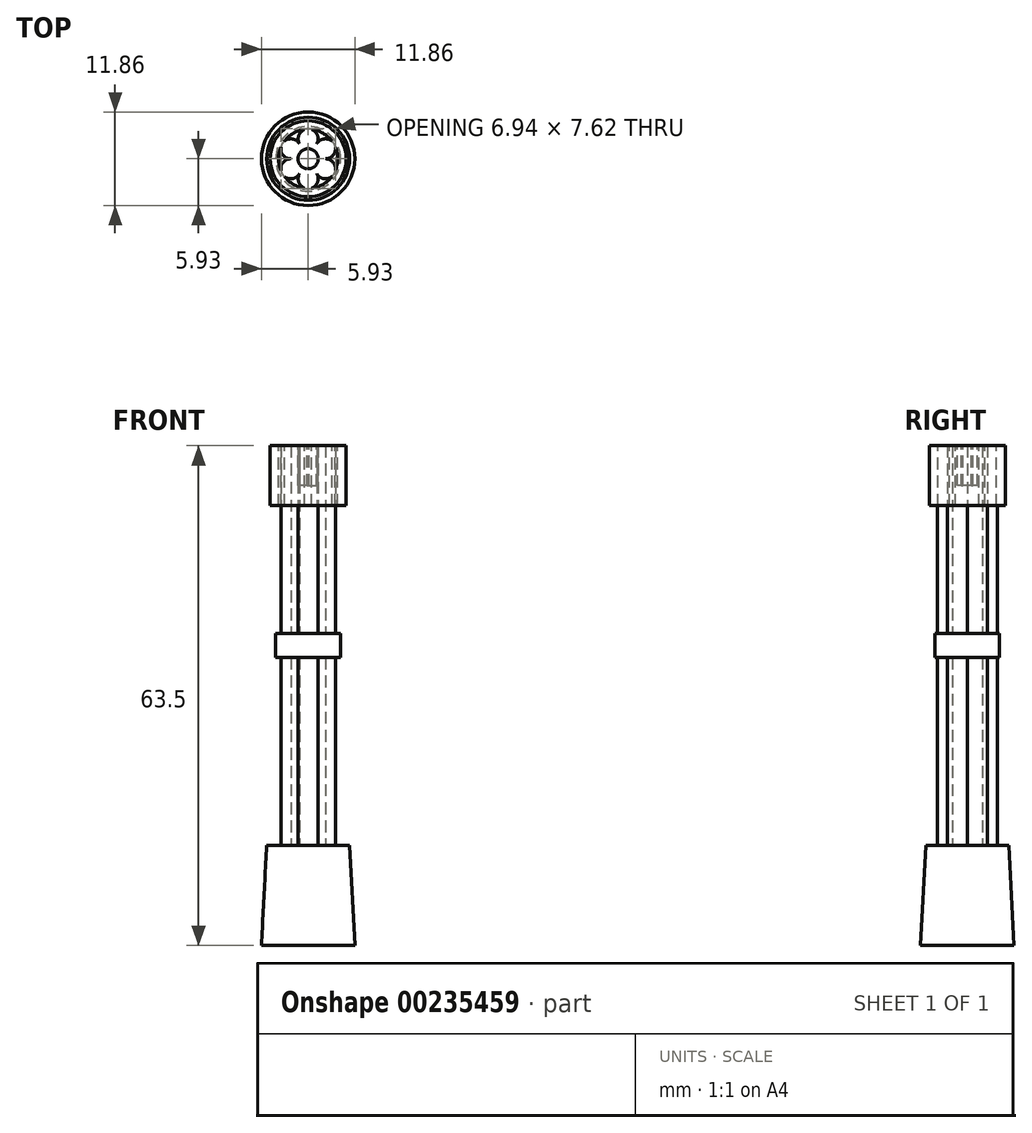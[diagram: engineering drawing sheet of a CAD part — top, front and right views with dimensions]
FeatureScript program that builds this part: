
annotation { "Feature Type Name" : "Feature", "Feature Type Description" : "" }
export const myFeature = defineFeature(function(context is Context, id is Id, definition is map)
    precondition{}
    {
        {
            var Q0;
            Q0=qCreatedBy(makeId("Top.planeOp"),FACE);
            var sketch = newSketch(context, id + "F0", { "sketchPlane" : qUnion([Q0])});
            skCircle(sketch, "E0", {"center": v(0, 0) * mm, "radius": 1.27 * mm});
            skCircle(sketch, "E1", {"center": v(0, 2.54) * mm, "radius": 1.27 * mm});
            skCircle(sketch, "E2.1.0", {"center": v(-2.2, 1.27) * mm, "radius": 1.27 * mm});
            skCircle(sketch, "E2.2.0", {"center": v(-2.2, -1.27) * mm, "radius": 1.27 * mm});
            skCircle(sketch, "E2.3.0", {"center": v(0, -2.54) * mm, "radius": 1.27 * mm});
            skCircle(sketch, "E2.4.0", {"center": v(2.2, -1.27) * mm, "radius": 1.27 * mm});
            skCircle(sketch, "E2.5.0", {"center": v(2.2, 1.27) * mm, "radius": 1.27 * mm});
            skCircle(sketch, "E3", {"center": v(0, 0) * mm, "radius": 3.81 * mm});
            skCircle(sketch, "E4", {"center": v(0, 0) * mm, "radius": 4.12 * mm});
            skSolve(sketch);
        }
        {
            var Q0;
            {var subQ0=sQuery(id+"F0.wireOp",EDGE,"E0");var subQ4=makeQuery(id+"F0.imprint","INTERSECT",VERTEX,{"derivedFrom":[subQ0,sQuery(id+"F0.wireOp",EDGE,"E1")]});Q0=makeQuery(id+"F0.imprint","IMPRINT",FACE,{"disambiguationData":[TD([[makeQuery(id+"F0.imprint","IMPRINT",EDGE,{"disambiguationData":[TD([[subQ4,1.0]])],"derivedFrom":subQ0}),1.0]])]});}
            var Q1;
            {var subQ0=sQuery(id+"F0.wireOp",EDGE,"E1");var subQ1=sQuery(id+"F0.wireOp",EDGE,"E0");var subQ2=makeQuery(id+"F0.imprint","INTERSECT",VERTEX,{"derivedFrom":[subQ1,subQ0]});Q1=makeQuery(id+"F0.imprint","IMPRINT",FACE,{"disambiguationData":[TD([[makeQuery(id+"F0.imprint","IMPRINT",EDGE,{"disambiguationData":[TD([[subQ2,-1.0]])],"derivedFrom":subQ1}),-1.0]])]});}
            var Q2;
            {var subQ0=sQuery(id+"F0.wireOp",EDGE,"E1");var subQ1=sQuery(id+"F0.wireOp",EDGE,"E0");var subQ2=makeQuery(id+"F0.imprint","INTERSECT",VERTEX,{"derivedFrom":[subQ1,subQ0]});Q2=makeQuery(id+"F0.imprint","IMPRINT",FACE,{"disambiguationData":[TD([[makeQuery(id+"F0.imprint","IMPRINT",EDGE,{"disambiguationData":[TD([[subQ2,1.0]])],"derivedFrom":subQ1}),-1.0]])]});}
            var Q3;
            {var subQ0=sQuery(id+"F0.wireOp",EDGE,"E2.5.0");var subQ1=sQuery(id+"F0.wireOp",EDGE,"E0");var subQ2=makeQuery(id+"F0.imprint","INTERSECT",VERTEX,{"derivedFrom":[subQ1,subQ0]});Q3=makeQuery(id+"F0.imprint","IMPRINT",FACE,{"disambiguationData":[TD([[makeQuery(id+"F0.imprint","IMPRINT",EDGE,{"disambiguationData":[TD([[subQ2,1.0]])],"derivedFrom":subQ1}),-1.0]])]});}
            var Q4;
            {var subQ0=sQuery(id+"F0.wireOp",EDGE,"E2.3.0");var subQ1=sQuery(id+"F0.wireOp",EDGE,"E0");var subQ2=makeQuery(id+"F0.imprint","INTERSECT",VERTEX,{"derivedFrom":[subQ1,subQ0]});Q4=makeQuery(id+"F0.imprint","IMPRINT",FACE,{"disambiguationData":[TD([[makeQuery(id+"F0.imprint","IMPRINT",EDGE,{"disambiguationData":[TD([[subQ2,-1.0]])],"derivedFrom":subQ1}),-1.0]])]});}
            var Q5;
            {var subQ0=sQuery(id+"F0.wireOp",EDGE,"E2.2.0");var subQ1=sQuery(id+"F0.wireOp",EDGE,"E0");var subQ2=makeQuery(id+"F0.imprint","INTERSECT",VERTEX,{"derivedFrom":[subQ1,subQ0]});Q5=makeQuery(id+"F0.imprint","IMPRINT",FACE,{"disambiguationData":[TD([[makeQuery(id+"F0.imprint","IMPRINT",EDGE,{"disambiguationData":[TD([[subQ2,-1.0]])],"derivedFrom":subQ1}),-1.0]])]});}
            var Q6;
            {var subQ0=sQuery(id+"F0.wireOp",EDGE,"E2.1.0");var subQ1=sQuery(id+"F0.wireOp",EDGE,"E0");var subQ2=makeQuery(id+"F0.imprint","INTERSECT",VERTEX,{"derivedFrom":[subQ1,subQ0]});Q6=makeQuery(id+"F0.imprint","IMPRINT",FACE,{"disambiguationData":[TD([[makeQuery(id+"F0.imprint","IMPRINT",EDGE,{"disambiguationData":[TD([[subQ2,-1.0]])],"derivedFrom":subQ1}),-1.0]])]});}
            var Q7;
            {var subQ0=sQuery(id+"F0.wireOp",EDGE,"E1");var subQ1=makeQuery(id+"F0.imprint","INTERSECT",VERTEX,{"derivedFrom":[subQ0,sQuery(id+"F0.wireOp",EDGE,"E2.1.0")]});Q7=makeQuery(id+"F0.imprint","IMPRINT",FACE,{"disambiguationData":[TD([[makeQuery(id+"F0.imprint","IMPRINT",EDGE,{"disambiguationData":[TD([[subQ1,1.0]])],"derivedFrom":subQ0}),1.0]])]});}
            var Q8;
            {var subQ0=sQuery(id+"F0.wireOp",EDGE,"E2.1.0");var subQ1=makeQuery(id+"F0.imprint","INTERSECT",VERTEX,{"derivedFrom":[subQ0,sQuery(id+"F0.wireOp",EDGE,"E2.2.0")]});Q8=makeQuery(id+"F0.imprint","IMPRINT",FACE,{"disambiguationData":[TD([[makeQuery(id+"F0.imprint","IMPRINT",EDGE,{"disambiguationData":[TD([[subQ1,1.0]])],"derivedFrom":subQ0}),1.0]])]});}
            var Q9;
            {var subQ0=sQuery(id+"F0.wireOp",EDGE,"E2.2.0");var subQ1=makeQuery(id+"F0.imprint","INTERSECT",VERTEX,{"derivedFrom":[subQ0,sQuery(id+"F0.wireOp",EDGE,"E2.3.0")]});Q9=makeQuery(id+"F0.imprint","IMPRINT",FACE,{"disambiguationData":[TD([[makeQuery(id+"F0.imprint","IMPRINT",EDGE,{"disambiguationData":[TD([[subQ1,1.0]])],"derivedFrom":subQ0}),1.0]])]});}
            var Q10;
            {var subQ0=sQuery(id+"F0.wireOp",EDGE,"E2.3.0");var subQ1=makeQuery(id+"F0.imprint","INTERSECT",VERTEX,{"derivedFrom":[subQ0,sQuery(id+"F0.wireOp",EDGE,"E2.4.0")]});Q10=makeQuery(id+"F0.imprint","IMPRINT",FACE,{"disambiguationData":[TD([[makeQuery(id+"F0.imprint","IMPRINT",EDGE,{"disambiguationData":[TD([[subQ1,1.0]])],"derivedFrom":subQ0}),1.0]])]});}
            var Q11;
            {var subQ0=sQuery(id+"F0.wireOp",EDGE,"E2.4.0");var subQ1=makeQuery(id+"F0.imprint","INTERSECT",VERTEX,{"derivedFrom":[subQ0,sQuery(id+"F0.wireOp",EDGE,"E2.5.0")]});Q11=makeQuery(id+"F0.imprint","IMPRINT",FACE,{"disambiguationData":[TD([[makeQuery(id+"F0.imprint","IMPRINT",EDGE,{"disambiguationData":[TD([[subQ1,1.0]])],"derivedFrom":subQ0}),1.0]])]});}
            var Q12;
            {var subQ0=sQuery(id+"F0.wireOp",EDGE,"E2.5.0");var subQ1=makeQuery(id+"F0.imprint","INTERSECT",VERTEX,{"derivedFrom":[sQuery(id+"F0.wireOp",EDGE,"E1"),subQ0]});Q12=makeQuery(id+"F0.imprint","IMPRINT",FACE,{"disambiguationData":[TD([[makeQuery(id+"F0.imprint","IMPRINT",EDGE,{"disambiguationData":[TD([[subQ1,1.0]])],"derivedFrom":subQ0}),1.0]])]});}
            extrude(context, id + "F1", {"entities" : qUnion([Q0, Q1, Q2, Q3, Q4, Q5, Q6, Q7, Q8, Q9, Q10, Q11, Q12]), "endBound" : BoundingType.SYMMETRIC, "depth" : 50.8 * mm});
        }
        {
            var Q0;
            {var subQ0=sQuery(id+"F0.wireOp",EDGE,"E2.1.0");var subQ1=sQuery(id+"F0.wireOp",EDGE,"E1");var subQ2=makeQuery(id+"F0.imprint","INTERSECT",VERTEX,{"derivedFrom":[subQ1,subQ0]});Q0=makeQuery(id+"F0.imprint","IMPRINT",FACE,{"disambiguationData":[TD([[makeQuery(id+"F0.imprint","IMPRINT",EDGE,{"disambiguationData":[TD([[subQ2,1.0]])],"derivedFrom":subQ1}),-1.0]])]});}
            var Q1;
            {var subQ0=sQuery(id+"F0.wireOp",EDGE,"E3");var subQ1=sQuery(id+"F0.wireOp",EDGE,"E1");var subQ2=makeQuery(id+"F0.imprint","INTERSECT",VERTEX,{"derivedFrom":[subQ1,subQ0]});Q1=makeQuery(id+"F0.imprint","IMPRINT",FACE,{"disambiguationData":[TD([[makeQuery(id+"F0.imprint","IMPRINT",EDGE,{"disambiguationData":[TD([[subQ2,1.0]])],"derivedFrom":subQ1}),-1.0]])]});}
            var Q2;
            {var subQ0=sQuery(id+"F0.wireOp",EDGE,"E2.5.0");var subQ1=sQuery(id+"F0.wireOp",EDGE,"E2.4.0");var subQ2=makeQuery(id+"F0.imprint","INTERSECT",VERTEX,{"derivedFrom":[subQ1,subQ0]});Q2=makeQuery(id+"F0.imprint","IMPRINT",FACE,{"disambiguationData":[TD([[makeQuery(id+"F0.imprint","IMPRINT",EDGE,{"disambiguationData":[TD([[subQ2,1.0]])],"derivedFrom":subQ1}),-1.0]])]});}
            var Q3;
            {var subQ0=sQuery(id+"F0.wireOp",EDGE,"E2.4.0");var subQ1=sQuery(id+"F0.wireOp",EDGE,"E2.3.0");var subQ2=makeQuery(id+"F0.imprint","INTERSECT",VERTEX,{"derivedFrom":[subQ1,subQ0]});Q3=makeQuery(id+"F0.imprint","IMPRINT",FACE,{"disambiguationData":[TD([[makeQuery(id+"F0.imprint","IMPRINT",EDGE,{"disambiguationData":[TD([[subQ2,1.0]])],"derivedFrom":subQ1}),-1.0]])]});}
            var Q4;
            {var subQ0=sQuery(id+"F0.wireOp",EDGE,"E2.3.0");var subQ1=sQuery(id+"F0.wireOp",EDGE,"E2.2.0");var subQ2=makeQuery(id+"F0.imprint","INTERSECT",VERTEX,{"derivedFrom":[subQ1,subQ0]});Q4=makeQuery(id+"F0.imprint","IMPRINT",FACE,{"disambiguationData":[TD([[makeQuery(id+"F0.imprint","IMPRINT",EDGE,{"disambiguationData":[TD([[subQ2,1.0]])],"derivedFrom":subQ1}),-1.0]])]});}
            var Q5;
            {var subQ0=sQuery(id+"F0.wireOp",EDGE,"E2.2.0");var subQ1=sQuery(id+"F0.wireOp",EDGE,"E2.1.0");var subQ2=makeQuery(id+"F0.imprint","INTERSECT",VERTEX,{"derivedFrom":[subQ1,subQ0]});Q5=makeQuery(id+"F0.imprint","IMPRINT",FACE,{"disambiguationData":[TD([[makeQuery(id+"F0.imprint","IMPRINT",EDGE,{"disambiguationData":[TD([[subQ2,1.0]])],"derivedFrom":subQ1}),-1.0]])]});}
            var Q6;
            Q6=makeQuery(id+"F0.imprint","IMPRINT",FACE,{"disambiguationData":[TD([[makeQuery(id+"F0.imprint","IMPRINT",EDGE,{"derivedFrom":sQuery(id+"F0.wireOp",EDGE,"E4")}),1.0]])]});
            extrude(context, id + "F2", {"entities" : qUnion([Q0, Q1, Q2, Q3, Q4, Q5, Q6]), "operationType" : NewBodyOperationType.ADD, "endBound" : BoundingType.SYMMETRIC, "depth" : 3.05 * mm});
        }
        {
            var Q0;
            Q0=makeQuery(id+"F1.opExtrude","CAP_FACE",FACE,{"disambiguationData":[OSD([sQuery(id+"F0.wireOp",EDGE,"E1"),sQuery(id+"F0.wireOp",EDGE,"E2.1.0"),sQuery(id+"F0.wireOp",EDGE,"E2.2.0"),sQuery(id+"F0.wireOp",EDGE,"E2.3.0"),sQuery(id+"F0.wireOp",EDGE,"E2.4.0"),sQuery(id+"F0.wireOp",EDGE,"E2.5.0")])],"isStart":false});
            var sketch = newSketch(context, id + "F3", { "sketchPlane" : qUnion([Q0])});
            skCircle(sketch, "E5", {"center": v(0, 0) * mm, "radius": 1.28 * mm});
            skCircle(sketch, "E6", {"center": v(0, 2.54) * mm, "radius": 1.27 * mm});
            skCircle(sketch, "E7.1.0", {"center": v(-2.2, 1.27) * mm, "radius": 1.27 * mm});
            skCircle(sketch, "E7.2.0", {"center": v(-2.2, -1.27) * mm, "radius": 1.27 * mm});
            skCircle(sketch, "E7.3.0", {"center": v(0, -2.54) * mm, "radius": 1.27 * mm});
            skCircle(sketch, "E7.4.0", {"center": v(2.2, -1.27) * mm, "radius": 1.27 * mm});
            skCircle(sketch, "E7.5.0", {"center": v(2.2, 1.27) * mm, "radius": 1.27 * mm});
            skSolve(sketch);
        }
        {
            var Q0;
            {var subQ1=sQuery(id+"F3.wireOp",EDGE,"E5");var subQ4=sQuery(id+"F3.wireOp",EDGE,"E7.5.0");var subQ15=makeQuery(id+"F3.imprint","INTERSECT",VERTEX,{"disambiguationData":[OD(0.0)],"derivedFrom":[subQ1,subQ4]});Q0=makeQuery(id+"F3.imprint","IMPRINT",FACE,{"disambiguationData":[TD([[makeQuery(id+"F3.imprint","IMPRINT",EDGE,{"disambiguationData":[TD([[subQ15,-1.0]])],"derivedFrom":subQ1}),1.0]])]});}
            extrude(context, id + "F4", {"entities" : qUnion([Q0]), "operationType" : NewBodyOperationType.REMOVE, "oppositeDirection" : true, "depth" : 5.08 * mm});
        }
        {
            var Q0;
            {var subQ0=sQuery(id+"F3.wireOp",EDGE,"E6");var subQ1=sQuery(id+"F3.wireOp",EDGE,"E5");var subQ2=makeQuery(id+"F3.imprint","INTERSECT",VERTEX,{"disambiguationData":[OD(0.0)],"derivedFrom":[subQ1,subQ0]});Q0=makeQuery(id+"F3.imprint","IMPRINT",FACE,{"disambiguationData":[TD([[makeQuery(id+"F3.imprint","IMPRINT",EDGE,{"disambiguationData":[TD([[subQ2,-1.0]])],"derivedFrom":subQ1}),-1.0]])]});}
            var sketch = newSketch(context, id + "F5", { "sketchPlane" : qUnion([Q0])});
            skCircle(sketch, "E8", {"center": v(0, 0) * mm, "radius": 4.83 * mm});
            skCircle(sketch, "E9", {"center": v(0, 0) * mm, "radius": 3.76 * mm});
            skSolve(sketch);
        }
        {
            var Q0;
            Q0=makeQuery(id+"F5.imprint","IMPRINT",FACE,{"disambiguationData":[TD([[makeQuery(id+"F5.imprint","IMPRINT",EDGE,{"derivedFrom":sQuery(id+"F5.wireOp",EDGE,"E8")}),1.0]])]});
            extrude(context, id + "F6", {"entities" : qUnion([Q0]), "operationType" : NewBodyOperationType.ADD, "oppositeDirection" : true, "depth" : 7.62 * mm});
        }
        {
            var Q0;
            Q0=makeQuery(id+"F1.opExtrude","CAP_FACE",FACE,{"disambiguationData":[OSD([sQuery(id+"F0.wireOp",EDGE,"E1"),sQuery(id+"F0.wireOp",EDGE,"E2.1.0"),sQuery(id+"F0.wireOp",EDGE,"E2.2.0"),sQuery(id+"F0.wireOp",EDGE,"E2.3.0"),sQuery(id+"F0.wireOp",EDGE,"E2.4.0"),sQuery(id+"F0.wireOp",EDGE,"E2.5.0")])],"isStart":true});
            cPlane(context, id + "F7", {"entities" : qUnion([Q0]), "cplaneType" : CPlaneType.OFFSET, "offset" : 0 * mm, "width" : 152.4 * mm, "height" : 152.4 * mm});
        }
        {
            var Q0;
            Q0=qCreatedBy(id+"F7.planeOp",FACE);
            var sketch = newSketch(context, id + "F8", { "sketchPlane" : qUnion([Q0])});
            skCircle(sketch, "E10", {"center": v(0, 0) * mm, "radius": 5.27 * mm});
            skSolve(sketch);
        }
        {
            var Q0;
            Q0=makeQuery(id+"F8.imprint","IMPRINT",FACE,{"disambiguationData":[TD([[makeQuery(id+"F8.imprint","IMPRINT",EDGE,{"derivedFrom":sQuery(id+"F8.wireOp",EDGE,"E10")}),1.0]])]});
            extrude(context, id + "F9", {"entities" : qUnion([Q0]), "operationType" : NewBodyOperationType.ADD, "depth" : 12.7 * mm, "hasDraft" : true, "draftAngle" : 3 * degree});
        }
    });
